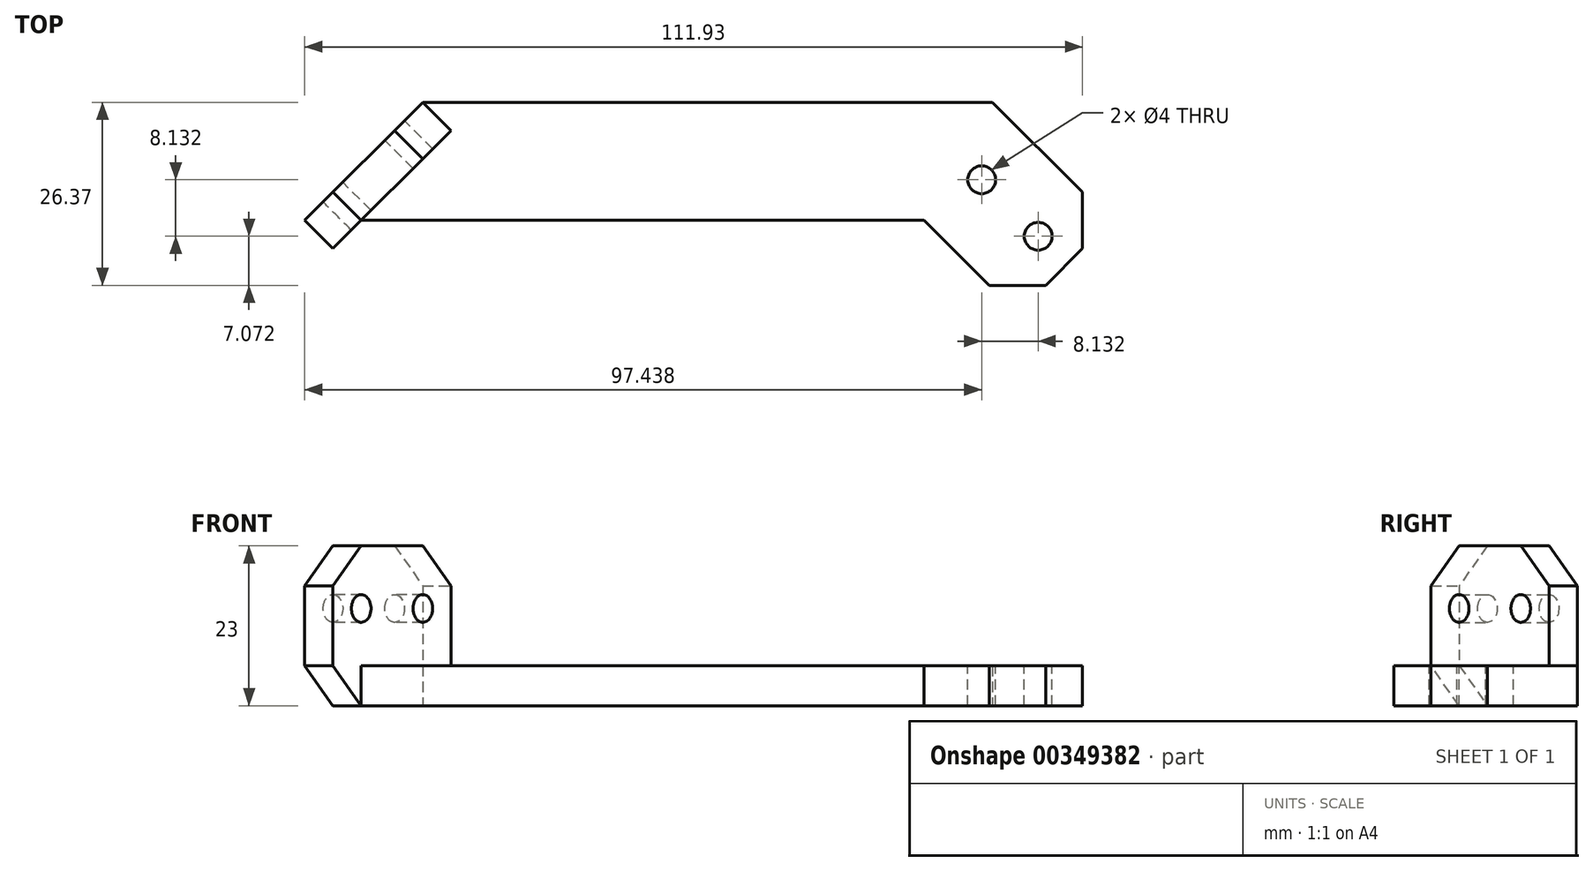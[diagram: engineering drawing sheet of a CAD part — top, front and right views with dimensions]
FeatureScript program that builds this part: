
annotation { "Feature Type Name" : "Feature", "Feature Type Description" : "" }
export const myFeature = defineFeature(function(context is Context, id is Id, definition is map)
    precondition{}
    {
        {
            var Q0;
            Q0=qCreatedBy(makeId("Top.planeOp"),FACE);
            var sketch = newSketch(context, id + "F0", { "sketchPlane" : qUnion([Q0])});
            skLineSegment(sketch, "E0.bottom", {"start": v(41, -8.5) * mm, "end": v(-41, -8.5) * mm});
            skLineSegment(sketch, "E0.top", {"start": v(41, 8.5) * mm, "end": v(-41, 8.5) * mm});
            skLineSegment(sketch, "E0.left", {"start": v(41, -8.5) * mm, "end": v(41, 8.5) * mm});
            skLineSegment(sketch, "E0.right", {"start": v(-41, -8.5) * mm, "end": v(-41, 8.5) * mm});
            skPoint(sketch, "E0.middle", {"position": v(0, 0) * mm});
            skLineSegment(sketch, "E1", {"start": v(-41, 8.5) * mm, "end": v(-58, -8.5) * mm});
            skLineSegment(sketch, "E2", {"start": v(-58, -8.5) * mm, "end": v(-41, -8.5) * mm});
            skLineSegment(sketch, "E3", {"start": v(41, 8.5) * mm, "end": v(58, -8.5) * mm});
            skLineSegment(sketch, "E4", {"start": v(58, -8.5) * mm, "end": v(41, -8.5) * mm});
            skSolve(sketch);
        }
        {
            var Q0;
            Q0 = qSketchRegion(id + "F0", true);
            extrude(context, id + "F1", {"entities" : qUnion([Q0]), "depth" : 5.75 * mm});
        }
        {
            var Q0;
            Q0=makeQuery(id+"F1.opExtrude","SWEPT_FACE",FACE,{"disambiguationData":[OSD([sQuery(id+"F0.wireOp",EDGE,"E1")])]});
            var sketch = newSketch(context, id + "F2", { "sketchPlane" : qUnion([Q0])});
            skLineSegment(sketch, "E5.bottom", {"start": v(22.98, 0) * mm, "end": v(47.02, 0) * mm});
            skLineSegment(sketch, "E5.top", {"start": v(22.98, 23) * mm, "end": v(47.02, 23) * mm});
            skLineSegment(sketch, "E5.left", {"start": v(22.98, 0) * mm, "end": v(22.98, 23) * mm});
            skLineSegment(sketch, "E5.right", {"start": v(47.02, 0) * mm, "end": v(47.02, 23) * mm});
            skSolve(sketch);
        }
        {
            var Q0;
            Q0 = qSketchRegion(id + "F2", true);
            extrude(context, id + "F3", {"entities" : qUnion([Q0]), "operationType" : NewBodyOperationType.ADD, "oppositeDirection" : true, "depth" : 5.75 * mm});
        }
        {
            var Q0;
            Q0=makeQuery(id+"F3.boolean.opBoolean","MERGE",FACE,{"derivedFrom":[makeQuery(id+"F1.opExtrude","SWEPT_FACE",FACE,{"disambiguationData":[OSD([sQuery(id+"F0.wireOp",EDGE,"E1")])]}),makeQuery(id+"F3.opExtrude","CAP_FACE",FACE,{"disambiguationData":[OSD([sQuery(id+"F2.wireOp",EDGE,"E5.bottom"),sQuery(id+"F2.wireOp",EDGE,"E5.top"),sQuery(id+"F2.wireOp",EDGE,"E5.left"),sQuery(id+"F2.wireOp",EDGE,"E5.right")])],"isStart":true})]});
            var sketch = newSketch(context, id + "F4", { "sketchPlane" : qUnion([Q0])});
            skCircle(sketch, "E6", {"center": v(28.73, 14) * mm, "radius": 2 * mm});
            skCircle(sketch, "E7", {"center": v(41.27, 14) * mm, "radius": 2 * mm});
            skSolve(sketch);
        }
        {
            var Q0;
            Q0 = qSketchRegion(id + "F4", true);
            extrude(context, id + "F5", {"entities" : qUnion([Q0]), "operationType" : NewBodyOperationType.REMOVE, "oppositeDirection" : true, "depth" : 25 * mm});
        }
        {
            var Q0;
            Q0=makeQuery(id+"F3.opExtrude","SWEPT_EDGE",EDGE,{"disambiguationData":[OSD([sQuery(id+"F2.wireOp",EDGE,"E5.top"),sQuery(id+"F2.wireOp",EDGE,"E5.right")])]});
            var Q1;
            Q1=makeQuery(id+"F3.opExtrude","SWEPT_EDGE",EDGE,{"disambiguationData":[OSD([sQuery(id+"F2.wireOp",EDGE,"E5.top"),sQuery(id+"F2.wireOp",EDGE,"E5.left")])]});
            var Q2;
            Q2=makeQuery(id+"F3.opExtrude","SWEPT_EDGE",EDGE,{"disambiguationData":[OSD([sQuery(id+"F2.wireOp",EDGE,"E5.bottom"),sQuery(id+"F2.wireOp",EDGE,"E5.right")])]});
            chamfer(context, id + "F6", {"entities" : qUnion([Q0, Q1, Q2]), "width" : (23 / 4) * mm, "tangentPropagation" : true});
        }
        {
            var Q0;
            Q0=makeQuery(id+"F1.opExtrude","CAP_FACE",FACE,{"disambiguationData":[OSD([sQuery(id+"F0.wireOp",EDGE,"E0.bottom"),sQuery(id+"F0.wireOp",EDGE,"E0.top"),sQuery(id+"F0.wireOp",EDGE,"E1"),sQuery(id+"F0.wireOp",EDGE,"E2"),sQuery(id+"F0.wireOp",EDGE,"E3"),sQuery(id+"F0.wireOp",EDGE,"E4")])],"isStart":false});
            var sketch = newSketch(context, id + "F7", { "sketchPlane" : qUnion([Q0])});
            skLineSegment(sketch, "E8", {"start": v(41, 8.5) * mm, "end": v(28.3, -5.67) * mm});
            skLineSegment(sketch, "E9", {"start": v(28.3, -5.67) * mm, "end": v(44.56, -21.94) * mm});
            skLineSegment(sketch, "E10", {"start": v(44.56, -21.94) * mm, "end": v(58, -8.5) * mm});
            skLineSegment(sketch, "E11", {"start": v(58, -8.5) * mm, "end": v(41, 8.5) * mm});
            skSolve(sketch);
        }
        {
            var Q0;
            {var subQ0=sQuery(id+"F7.wireOp",EDGE,"E9");Q0=makeQuery(id+"F7.imprint","IMPRINT",FACE,{"disambiguationData":[TD([[makeQuery(id+"F7.imprint","IMPRINT",EDGE,{"derivedFrom":subQ0}),1.0]])]});}
            extrude(context, id + "F8", {"entities" : qUnion([Q0]), "operationType" : NewBodyOperationType.ADD, "oppositeDirection" : true, "depth" : 5.75 * mm});
        }
        {
            var Q0;
            {var subQ0=sQuery(id+"F0.wireOp",EDGE,"E4");var subQ1=sQuery(id+"F0.wireOp",EDGE,"E2");var subQ2=sQuery(id+"F0.wireOp",EDGE,"E0.bottom");Q0=makeQuery(id+"F8.boolean.opBoolean","MERGE",FACE,{"derivedFrom":[makeQuery(id+"F1.opExtrude","CAP_FACE",FACE,{"disambiguationData":[OSD([subQ2,sQuery(id+"F0.wireOp",EDGE,"E0.top"),sQuery(id+"F0.wireOp",EDGE,"E1"),subQ1,sQuery(id+"F0.wireOp",EDGE,"E3"),subQ0])],"isStart":false}),makeQuery(id+"F8.opExtrude","CAP_FACE",FACE,{"disambiguationData":[OSD([subQ2,subQ1,subQ0,sQuery(id+"F7.wireOp",EDGE,"E9"),sQuery(id+"F7.wireOp",EDGE,"E10")])],"isStart":true})]});}
            var sketch = newSketch(context, id + "F9", { "sketchPlane" : qUnion([Q0])});
            skCircle(sketch, "E12", {"center": v(47.57, -10.8) * mm, "radius": 2 * mm});
            skCircle(sketch, "E13", {"center": v(39.44, -2.67) * mm, "radius": 2 * mm});
            skSolve(sketch);
        }
        {
            var Q0;
            Q0 = qSketchRegion(id + "F9", true);
            extrude(context, id + "F10", {"entities" : qUnion([Q0]), "operationType" : NewBodyOperationType.REMOVE, "oppositeDirection" : true, "depth" : 25 * mm});
        }
        {
            var Q0;
            Q0=makeQuery(id+"F8.opExtrude","SWEPT_EDGE",EDGE,{"disambiguationData":[OSD([sQuery(id+"F7.wireOp",EDGE,"E9"),sQuery(id+"F7.wireOp",EDGE,"E10")])]});
            var Q1;
            {var subQ0=sQuery(id+"F0.wireOp",EDGE,"E4");Q1=makeQuery(id+"F8.boolean.opBoolean","MERGE",EDGE,{"derivedFrom":[makeQuery(id+"F1.opExtrude","SWEPT_EDGE",EDGE,{"disambiguationData":[OSD([sQuery(id+"F0.wireOp",EDGE,"E3"),subQ0])]}),makeQuery(id+"F8.opExtrude","SWEPT_EDGE",EDGE,{"disambiguationData":[OSD([sQuery(id+"F0.wireOp",EDGE,"E0.bottom"),sQuery(id+"F0.wireOp",EDGE,"E2"),subQ0,sQuery(id+"F7.wireOp",EDGE,"E10"),sQuery(id+"F7.wireOp",EDGE,"E11")])]})]});}
            chamfer(context, id + "F11", {"entities" : qUnion([Q0, Q1]), "width" : (23 / 4) * mm, "tangentPropagation" : true});
        }
    });
